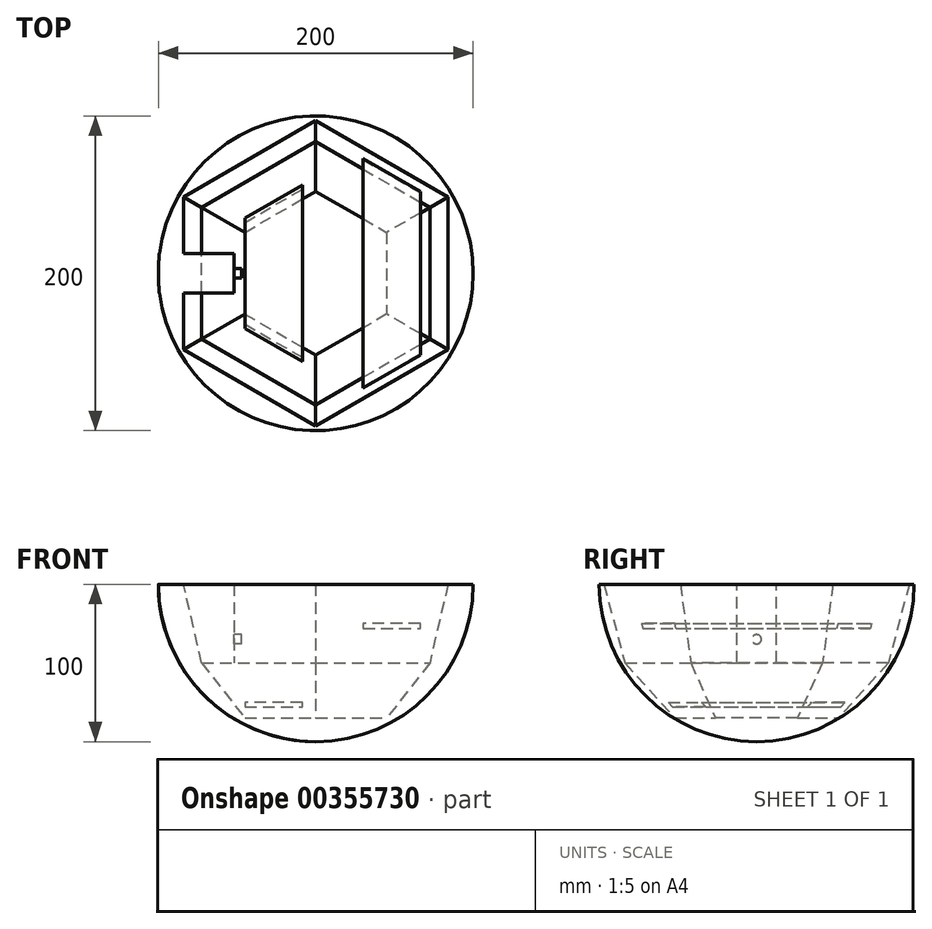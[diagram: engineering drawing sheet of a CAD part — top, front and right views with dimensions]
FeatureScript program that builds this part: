
annotation { "Feature Type Name" : "Feature", "Feature Type Description" : "" }
export const myFeature = defineFeature(function(context is Context, id is Id, definition is map)
    precondition{}
    {
        {
            var Q0;
            Q0=qCreatedBy(makeId("Front.planeOp"),FACE);
            var sketch = newSketch(context, id + "F0", { "sketchPlane" : qUnion([Q0])});
            skArc(sketch, "E0", {"start": v(-86.6, -50) * mm, "mid": v(-50, -86.6) * mm, "end": v(0, -100) * mm});
            skLineSegment(sketch, "E1", {"start": v(-86.6, -50) * mm, "end": v(0, -50) * mm});
            skLineSegment(sketch, "E2", {"start": v(0, -50) * mm, "end": v(0, -100) * mm});
            skLineSegment(sketch, "E3.trimOffspring", {"start": v(72.52, -50) * mm, "end": v(86.6, -50) * mm});
            skSolve(sketch);
        }
        {
            var Q0;
            Q0=makeQuery(id+"F0.imprint","IMPRINT",FACE,{"disambiguationData":[TD([[makeQuery(id+"F0.imprint","IMPRINT",EDGE,{"derivedFrom":sQuery(id+"F0.wireOp",EDGE,"E0")}),1.0]])]});
            var Q1;
            Q1=sQuery(id+"F0.wireOp",EDGE,"E2");
            revolve(context, id + "F1", {"entities" : qUnion([Q0]), "axis" : qUnion([Q1]), "revolveType" : RevolveType.FULL});
        }
        {
            var Q0;
            Q0=qCreatedBy(makeId("Top.planeOp"),FACE);
            cPlane(context, id + "F2", {"entities" : qUnion([Q0]), "cplaneType" : CPlaneType.OFFSET, "offset" : 44 * mm, "oppositeDirection" : true, "width" : 150 * mm, "height" : 150 * mm});
        }
        {
            var Q0;
            Q0=makeQuery(id+"F1.opRevolve","SWEPT_FACE",FACE,{"disambiguationData":[OSD([sQuery(id+"F0.wireOp",EDGE,"E1")])]});
            var sketch = newSketch(context, id + "F3", { "sketchPlane" : qUnion([Q0])});
            skCircle(sketch, "E4.cCircle", {"center": v(0, 0) * mm, "radius": 72.4 * mm, "construction": true});
            skLineSegment(sketch, "E4.0", {"start": v(72.4, -41.8) * mm, "end": v(0, -83.6) * mm});
            skLineSegment(sketch, "E4.1", {"start": v(0, -83.6) * mm, "end": v(-72.4, -41.8) * mm});
            skLineSegment(sketch, "E4.2", {"start": v(-72.4, -41.8) * mm, "end": v(-72.4, 41.8) * mm});
            skLineSegment(sketch, "E4.3", {"start": v(-72.4, 41.8) * mm, "end": v(0, 83.6) * mm});
            skLineSegment(sketch, "E4.4", {"start": v(0, 83.6) * mm, "end": v(72.4, 41.8) * mm});
            skLineSegment(sketch, "E4.5", {"start": v(72.4, 41.8) * mm, "end": v(72.4, -41.8) * mm});
            skPoint(sketch, "E4.0.midPoint", {"position": v(36.2, -62.7) * mm});
            skSolve(sketch);
        }
        {
            var Q0;
            Q0=makeQuery(id+"F3.imprint","IMPRINT",FACE,{"disambiguationData":[TD([[makeQuery(id+"F3.imprint","IMPRINT",EDGE,{"derivedFrom":sQuery(id+"F3.wireOp",EDGE,"E4.0")}),-1.0]])]});
            cPlane(context, id + "F4", {"entities" : qUnion([Q0]), "cplaneType" : CPlaneType.OFFSET, "offset" : 35 * mm, "oppositeDirection" : true, "width" : 150 * mm, "height" : 150 * mm});
        }
        {
            var Q0;
            Q0=qCreatedBy(id+"F4.planeOp",FACE);
            var sketch = newSketch(context, id + "F5", { "sketchPlane" : qUnion([Q0])});
            skCircle(sketch, "E5.cCircle", {"center": v(0, 0) * mm, "radius": 45.03 * mm, "construction": true});
            skLineSegment(sketch, "E5.0", {"start": v(0, 52) * mm, "end": v(45.03, 26) * mm});
            skLineSegment(sketch, "E5.1", {"start": v(45.03, 26) * mm, "end": v(45.03, -26) * mm});
            skLineSegment(sketch, "E5.2", {"start": v(45.03, -26) * mm, "end": v(0, -52) * mm});
            skLineSegment(sketch, "E5.3", {"start": v(0, -52) * mm, "end": v(-45.03, -26) * mm});
            skLineSegment(sketch, "E5.4", {"start": v(-45.03, -26) * mm, "end": v(-45.03, 26) * mm});
            skLineSegment(sketch, "E5.5", {"start": v(-45.03, 26) * mm, "end": v(0, 52) * mm});
            skPoint(sketch, "E5.0.midPoint", {"position": v(22.52, 39) * mm});
            skSolve(sketch);
        }
        {
            var Q1;
            Q1=makeQuery(id+"F3.imprint","IMPRINT",FACE,{"disambiguationData":[TD([[makeQuery(id+"F3.imprint","IMPRINT",EDGE,{"derivedFrom":sQuery(id+"F3.wireOp",EDGE,"E4.0")}),-1.0]])]});
            var Q2;
            Q2 = qSketchRegion(id + "F5", true);
            loft(context, id + "F6", {"operationType" : NewBodyOperationType.REMOVE, "sheetProfilesArray" : [{ "sheetProfileEntities" : qUnion([Q1]) }, { "sheetProfileEntities" : qUnion([Q2]) }]});
        }
        {
            var Q0;
            Q0=qCreatedBy(makeId("Front.planeOp"),FACE);
            var sketch = newSketch(context, id + "F7", { "sketchPlane" : qUnion([Q0])});
            skLineSegment(sketch, "E6.0", {"start": v(-86.6, -50) * mm, "end": v(0, -50) * mm});
            skLineSegment(sketch, "E7", {"start": v(0, 0) * mm, "end": v(0, -50) * mm});
            skLineSegment(sketch, "E8", {"start": v(0, 0) * mm, "end": v(-100, 0) * mm});
            skArc(sketch, "E9", {"start": v(-100, 0) * mm, "mid": v(-96.6, -25.88) * mm, "end": v(-86.6, -50) * mm});
            skPoint(sketch, "E10.orphan", {"position": v(86.6, -50) * mm});
            skSolve(sketch);
        }
        {
            var Q0;
            Q0=makeQuery(id+"F7.imprint","IMPRINT",FACE,{"disambiguationData":[TD([[makeQuery(id+"F7.imprint","IMPRINT",EDGE,{"derivedFrom":sQuery(id+"F7.wireOp",EDGE,"E6.0")}),1.0]])]});
            var Q1;
            Q1=sQuery(id+"F7.wireOp",EDGE,"E7");
            revolve(context, id + "F8", {"entities" : qUnion([Q0]), "axis" : qUnion([Q1]), "revolveType" : RevolveType.FULL});
        }
        {
            var Q0;
            Q0=makeQuery(id+"F8.opRevolve","SWEPT_FACE",FACE,{"disambiguationData":[OSD([sQuery(id+"F7.wireOp",EDGE,"E8")])]});
            var sketch = newSketch(context, id + "F9", { "sketchPlane" : qUnion([Q0])});
            skCircle(sketch, "E11.cCircle", {"center": v(0, 0) * mm, "radius": 84 * mm, "construction": true});
            skLineSegment(sketch, "E11.0", {"start": v(84, -48.5) * mm, "end": v(0, -97) * mm});
            skLineSegment(sketch, "E11.1", {"start": v(0, -97) * mm, "end": v(-84, -48.5) * mm});
            skLineSegment(sketch, "E11.2", {"start": v(-84, -48.5) * mm, "end": v(-84, 48.5) * mm});
            skLineSegment(sketch, "E11.3", {"start": v(-84, 48.5) * mm, "end": v(0, 97) * mm});
            skLineSegment(sketch, "E11.4", {"start": v(0, 97) * mm, "end": v(84, 48.5) * mm});
            skLineSegment(sketch, "E11.5", {"start": v(84, 48.5) * mm, "end": v(84, -48.5) * mm});
            skPoint(sketch, "E11.0.midPoint", {"position": v(42, -72.75) * mm});
            skSolve(sketch);
        }
        {
            var Q1;
            Q1=makeQuery(id+"F9.imprint","IMPRINT",FACE,{"disambiguationData":[TD([[makeQuery(id+"F9.imprint","IMPRINT",EDGE,{"derivedFrom":sQuery(id+"F9.wireOp",EDGE,"E11.0")}),-1.0]])]});
            var Q2;
            Q2 = qSketchRegion(id + "F3", true);
            loft(context, id + "F10", {"operationType" : NewBodyOperationType.REMOVE, "sheetProfilesArray" : [{ "sheetProfileEntities" : qUnion([Q1]) }, { "sheetProfileEntities" : qUnion([Q2]) }]});
        }
        {
            var Q0;
            Q0=qCreatedBy(makeId("Front.planeOp"),FACE);
            var sketch = newSketch(context, id + "F11", { "sketchPlane" : qUnion([Q0])});
            skLineSegment(sketch, "E12", {"start": v(-45.03, -75) * mm, "end": v(-8.53, -75) * mm});
            skLineSegment(sketch, "E13", {"start": v(-8.53, -75) * mm, "end": v(-8.53, -78) * mm});
            skLineSegment(sketch, "E14", {"start": v(-8.53, -78) * mm, "end": v(-45.03, -78) * mm});
            skLineSegment(sketch, "E15", {"start": v(-45.03, -78) * mm, "end": v(-45.03, -75) * mm});
            skSolve(sketch);
        }
        {
            var Q0;
            Q0=makeQuery(id+"F11.imprint","IMPRINT",FACE,{"disambiguationData":[TD([[makeQuery(id+"F11.imprint","IMPRINT",EDGE,{"derivedFrom":sQuery(id+"F11.wireOp",EDGE,"E12")}),-1.0]])]});
            var Q1;
            Q1=makeQuery(id+"F1.opRevolve","SWEPT_FACE",FACE,{"disambiguationData":[OSD([sQuery(id+"F0.wireOp",EDGE,"E0")])]});
            extrude(context, id + "F12", {"entities" : qUnion([Q0]), "operationType" : NewBodyOperationType.ADD, "endBound" : BoundingType.UP_TO_SURFACE, "endBoundEntityFace" : qUnion([Q1]), "depth" : 25 * mm});
        }
        {
            var Q0;
            Q0 = qSketchRegion(id + "F11", true);
            var Q1;
            Q1=makeQuery(id+"F1.opRevolve","SWEPT_FACE",FACE,{"disambiguationData":[OSD([sQuery(id+"F0.wireOp",EDGE,"E0")])]});
            extrude(context, id + "F13", {"entities" : qUnion([Q0]), "operationType" : NewBodyOperationType.ADD, "endBound" : BoundingType.UP_TO_SURFACE, "oppositeDirection" : true, "endBoundEntityFace" : qUnion([Q1]), "depth" : 25 * mm});
        }
        {
            var Q0;
            Q0=qCreatedBy(makeId("Front.planeOp"),FACE);
            var sketch = newSketch(context, id + "F14", { "sketchPlane" : qUnion([Q0])});
            skPoint(sketch, "E16.0", {"position": v(-72.4, -50) * mm});
            skPoint(sketch, "E17.0", {"position": v(72.4, -50) * mm});
            skPoint(sketch, "E18", {"position": v(-52, -50) * mm});
            skPoint(sketch, "E19", {"position": v(52, -50) * mm});
            skLineSegment(sketch, "E20", {"start": v(-99.48, 0) * mm, "end": v(-52, 0) * mm});
            skLineSegment(sketch, "E21", {"start": v(-52, 0) * mm, "end": v(-52, -50) * mm});
            skLineSegment(sketch, "E22", {"start": v(-72.4, -50) * mm, "end": v(-99.48, 0) * mm});
            skLineSegment(sketch, "E23", {"start": v(-72.4, -50) * mm, "end": v(-52, -50) * mm});
            skSolve(sketch);
        }
        {
            var Q0;
            Q0 = qSketchRegion(id + "F14", true);
            extrude(context, id + "F15", {"entities" : qUnion([Q0]), "operationType" : NewBodyOperationType.ADD, "endBound" : BoundingType.SYMMETRIC, "depth" : 25 * mm});
        }
        {
            var Q0;
            Q0=makeQuery(id+"F15.opExtrude","SWEPT_FACE",FACE,{"disambiguationData":[OSD([sQuery(id+"F14.wireOp",EDGE,"E21")])]});
            var sketch = newSketch(context, id + "F16", { "sketchPlane" : qUnion([Q0])});
            skCircle(sketch, "E24", {"center": v(0, -35) * mm, "radius": 3 * mm});
            skSolve(sketch);
        }
        {
            var Q0;
            Q0 = qSketchRegion(id + "F16", true);
            extrude(context, id + "F17", {"entities" : qUnion([Q0]), "operationType" : NewBodyOperationType.ADD, "depth" : 5 * mm});
        }
        {
            var Q0;
            Q0=qCreatedBy(makeId("Front.planeOp"),FACE);
            var sketch = newSketch(context, id + "F18", { "sketchPlane" : qUnion([Q0])});
            skLineSegment(sketch, "E25", {"start": v(30, -25) * mm, "end": v(66.5, -25) * mm});
            skLineSegment(sketch, "E26", {"start": v(66.5, -25) * mm, "end": v(66.5, -28) * mm});
            skLineSegment(sketch, "E27", {"start": v(66.5, -28) * mm, "end": v(30, -28) * mm});
            skLineSegment(sketch, "E28", {"start": v(30, -28) * mm, "end": v(30, -25) * mm});
            skSolve(sketch);
        }
        {
            var Q0;
            Q0=makeQuery(id+"F18.imprint","IMPRINT",FACE,{"disambiguationData":[TD([[makeQuery(id+"F18.imprint","IMPRINT",EDGE,{"derivedFrom":sQuery(id+"F18.wireOp",EDGE,"E25")}),-1.0]])]});
            var Q1;
            Q1=makeQuery(id+"F8.opRevolve","SWEPT_FACE",FACE,{"disambiguationData":[OSD([sQuery(id+"F7.wireOp",EDGE,"E9")])]});
            extrude(context, id + "F19", {"entities" : qUnion([Q0]), "operationType" : NewBodyOperationType.ADD, "endBound" : BoundingType.UP_TO_SURFACE, "endBoundEntityFace" : qUnion([Q1]), "depth" : 25 * mm});
        }
        {
            var Q0;
            Q0=makeQuery(id+"F19.opExtrude","CAP_FACE",FACE,{"disambiguationData":[OSD([sQuery(id+"F18.wireOp",EDGE,"E25"),sQuery(id+"F18.wireOp",EDGE,"E26"),sQuery(id+"F18.wireOp",EDGE,"E27"),sQuery(id+"F18.wireOp",EDGE,"E28")])],"isStart":true});
            var Q1;
            Q1=makeQuery(id+"F8.opRevolve","SWEPT_FACE",FACE,{"disambiguationData":[OSD([sQuery(id+"F7.wireOp",EDGE,"E9")])]});
            extrude(context, id + "F20", {"entities" : qUnion([Q0]), "operationType" : NewBodyOperationType.ADD, "endBound" : BoundingType.UP_TO_SURFACE, "endBoundEntityFace" : qUnion([Q1]), "depth" : 25 * mm});
        }
    });
